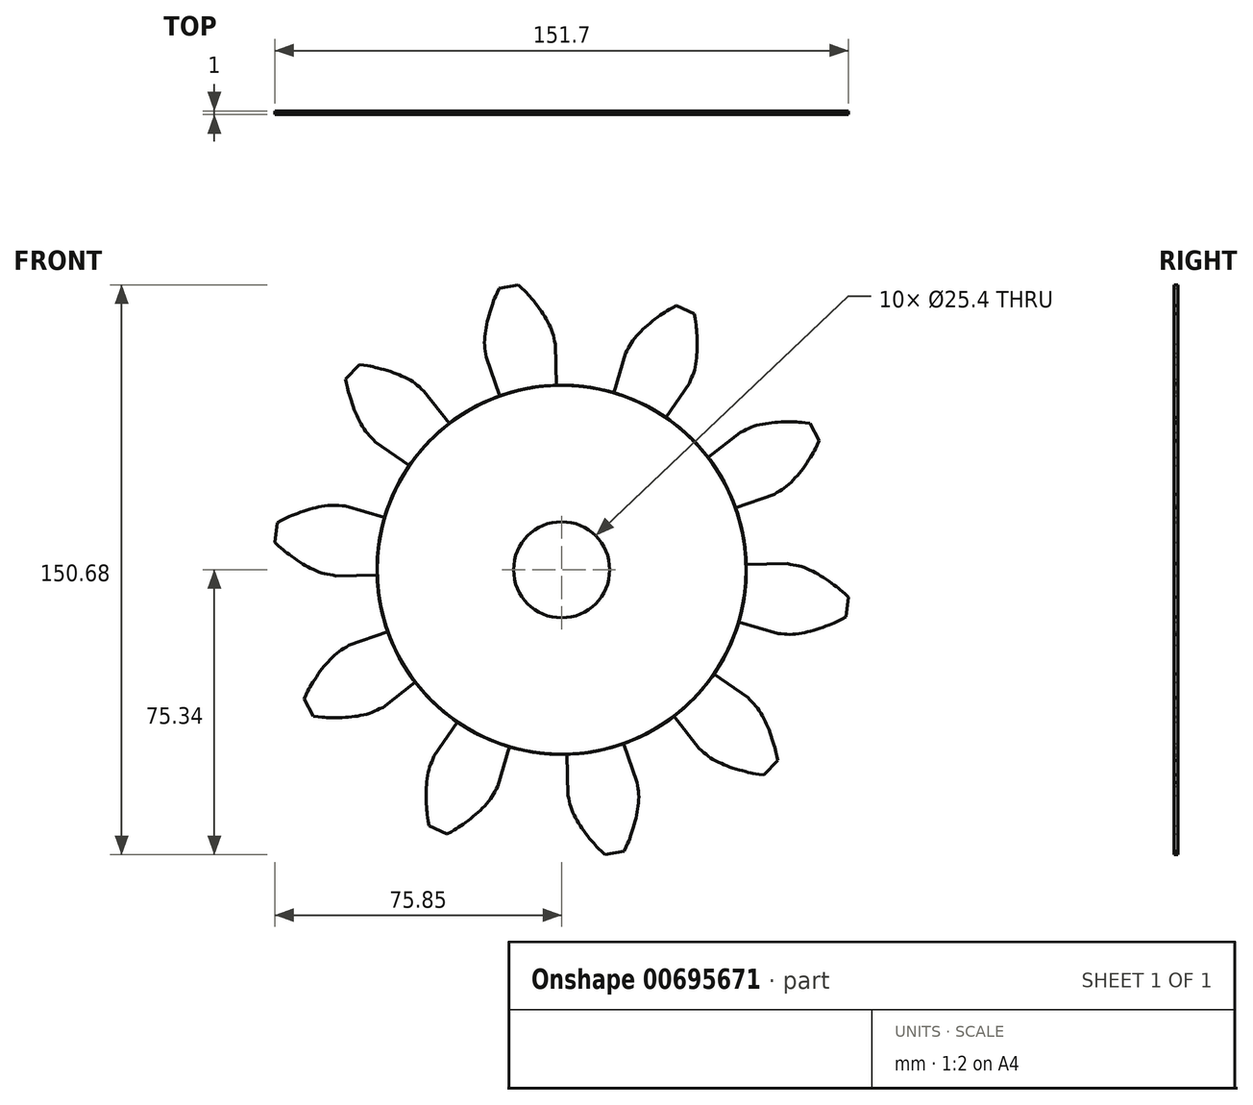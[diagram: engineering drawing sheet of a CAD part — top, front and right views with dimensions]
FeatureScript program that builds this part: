
annotation { "Feature Type Name" : "Feature", "Feature Type Description" : "" }
export const myFeature = defineFeature(function(context is Context, id is Id, definition is map)
    precondition{}
    {
        {
            assignVariable(context, id + "F0", {"name" : "Teeth", "anyValue" : 10});
        }
        {
            assignVariable(context, id + "F1", {"name" : "GearDepth", "anyValue" : 1});
        }
        {
            var Q0;
            Q0=qCreatedBy(makeId("Front.planeOp"),FACE);
            var sketch = newSketch(context, id + "F2", { "sketchPlane" : qUnion([Q0])});
            skCircle(sketch, "E0", {"center": v(0, 0) * mm, "radius": 76.2 * mm, "construction": true});
            skCircle(sketch, "E1", {"center": v(0, 0) * mm, "radius": 63.5 * mm, "construction": true});
            skCircle(sketch, "E2", {"center": v(0, 0) * mm, "radius": 59.67 * mm, "construction": true});
            skCircle(sketch, "E3", {"center": v(0, 0) * mm, "radius": 48.8 * mm});
            skCircle(sketch, "E4", {"center": v(0, 0) * mm, "radius": 12.7 * mm});
            skSolve(sketch);
        }
        {
            var Q0;
            Q0=makeQuery(id+"F2.imprint","IMPRINT",FACE,{"disambiguationData":[TD([[makeQuery(id+"F2.imprint","IMPRINT",EDGE,{"derivedFrom":sQuery(id+"F2.wireOp",EDGE,"E3")}),1.0]])]});
            var sketch = newSketch(context, id + "F3", { "sketchPlane" : qUnion([Q0])});
            skPoint(sketch, "E5", {"position": v(-1.64, 59.65) * mm});
            skPoint(sketch, "E6", {"position": v(-2.48, 62.93) * mm});
            skPoint(sketch, "E7", {"position": v(-4.01, 66.16) * mm});
            skPoint(sketch, "E8", {"position": v(-6.05, 69.32) * mm});
            skPoint(sketch, "E9", {"position": v(-8.53, 72.4) * mm});
            skPoint(sketch, "E10", {"position": v(-11.42, 75.34) * mm});
            skFitSpline(sketch, "E11", {"points": [v(-1.64, 59.65) * mm, v(-2.48, 62.93) * mm, v(-4.01, 66.16) * mm, v(-6.05, 69.32) * mm, v(-8.53, 72.4) * mm, v(-11.42, 75.34) * mm], "startDerivative": vector(-6.36, 19.59) * mm, "endDerivative": vector(-24.62, 23.26) * mm});
            skCircle(sketch, "E12.0", {"center": v(0, 0) * mm, "radius": 48.8 * mm});
            skLineSegment(sketch, "E13", {"start": v(-1.64, 59.65) * mm, "end": v(-1.34, 48.79) * mm});
            skCircle(sketch, "E14.0", {"center": v(0, 0) * mm, "radius": 76.2 * mm, "construction": true});
            skLineSegment(sketch, "E15", {"start": v(0, 0) * mm, "end": v(0, 76.2) * mm, "construction": true});
            skCircle(sketch, "E16.0", {"center": v(0, 0) * mm, "radius": 59.67 * mm, "construction": true});
            skLineSegment(sketch, "E17", {"start": v(0, 0) * mm, "end": v(-13.98, 74.9) * mm, "construction": true});
            skLineSegment(sketch, "E18", {"start": v(0, 0) * mm, "end": v(-1.64, 59.65) * mm, "construction": true});
            skFitSpline(sketch, "E19.MirrorCS", {"points": [v(-19.99, 56.22) * mm, v(-20.38, 59.59) * mm, v(-20.12, 63.15) * mm, v(-19.36, 66.84) * mm, v(-18.16, 70.6) * mm, v(-16.52, 74.39) * mm], "startDerivative": vector(-1.13, 20.56) * mm, "endDerivative": vector(14.57, 30.57) * mm});
            skLineSegment(sketch, "E20", {"start": v(-16.52, 74.39) * mm, "end": v(-11.42, 75.34) * mm});
            skLineSegment(sketch, "E21", {"start": v(-19.99, 56.22) * mm, "end": v(-16.35, 45.99) * mm});
            skCircle(sketch, "E22.0", {"center": v(0, 0) * mm, "radius": 12.7 * mm});
            skSolve(sketch);
        }
        {
            var Q0;
            Q0=qSketchRegion(id+"F3",true);
            extrude(context, id + "F4", {"entities" : qUnion([Q0]), "depth" : (getVariable(context, 'GearDepth')) * mm});
        }
        {
            var Q0;
            Q0=makeQuery(id+"F4.opExtrude","SWEPT_BODY",BODY,{"disambiguationData":[OSD([sQuery(id+"F3.wireOp",EDGE,"E11"),sQuery(id+"F3.wireOp",EDGE,"E12.0"),sQuery(id+"F3.wireOp",EDGE,"E13"),sQuery(id+"F3.wireOp",EDGE,"4b343bb4-83ff-42f4-a597-0c625fc55ac80.MirrorCS"),sQuery(id+"F3.wireOp",EDGE,"12547313-78bc-4742-a5d9-da1879d64cd0")])]});
            var Q1;
            Q1=sQuery(id+"F2.wireOp",EDGE,"E3");
            circularPattern(context, id + "F5", {"entities" : qUnion([Q0]), "axis" : qUnion([Q1]), "angle" : (360 / getVariable(context, 'Teeth')) * degree, "instanceCount" : getVariable(context, 'Teeth')});
        }
    });
